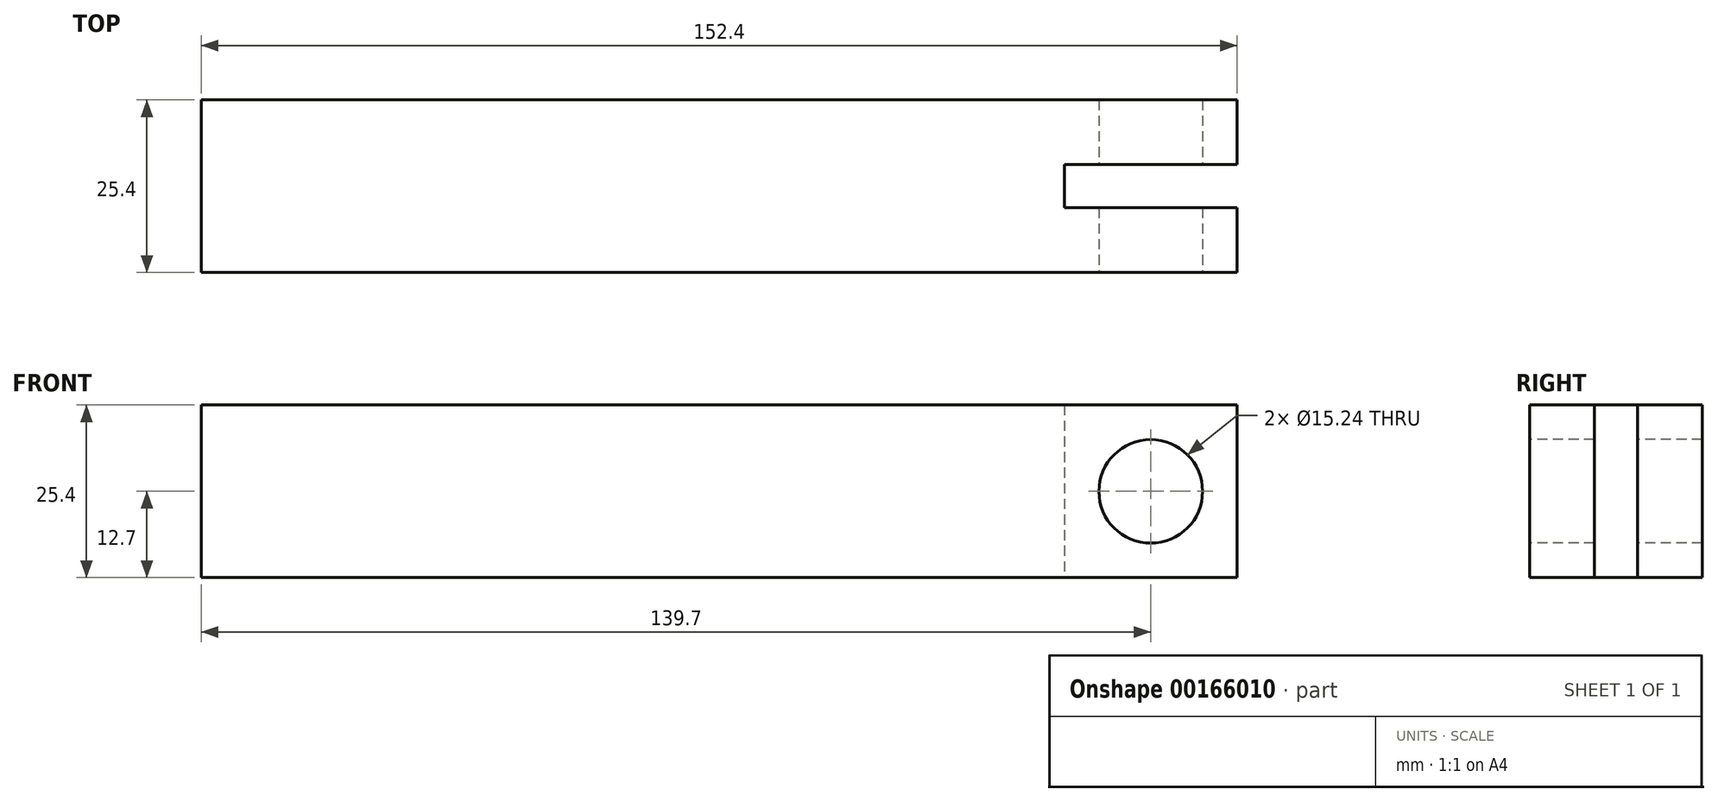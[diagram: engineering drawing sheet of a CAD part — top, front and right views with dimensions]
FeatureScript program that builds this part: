
annotation { "Feature Type Name" : "Feature", "Feature Type Description" : "" }
export const myFeature = defineFeature(function(context is Context, id is Id, definition is map)
    precondition{}
    {
        {
            var Q0;
            Q0=qCreatedBy(makeId("Right.planeOp"),FACE);
            var sketch = newSketch(context, id + "F0", { "sketchPlane" : qUnion([Q0])});
            skLineSegment(sketch, "E0.bottom", {"start": v(12.7, 12.7) * mm, "end": v(-12.7, 12.7) * mm});
            skLineSegment(sketch, "E0.top", {"start": v(12.7, -12.7) * mm, "end": v(-12.7, -12.7) * mm});
            skLineSegment(sketch, "E0.left", {"start": v(12.7, 12.7) * mm, "end": v(12.7, -12.7) * mm});
            skLineSegment(sketch, "E0.right", {"start": v(-12.7, 12.7) * mm, "end": v(-12.7, -12.7) * mm});
            skPoint(sketch, "E0.middle", {"position": v(0, 0) * mm});
            skSolve(sketch);
        }
        {
            var Q0;
            Q0 = qSketchRegion(id + "F0", true);
            extrude(context, id + "F1", {"entities" : qUnion([Q0]), "endBound" : BoundingType.SYMMETRIC, "depth" : 152.4 * mm});
        }
        {
            var Q0;
            Q0=makeQuery(id+"F1.opExtrude","SWEPT_FACE",FACE,{"disambiguationData":[OSD([sQuery(id+"F0.wireOp",EDGE,"E0.right")])]});
            var sketch = newSketch(context, id + "F2", { "sketchPlane" : qUnion([Q0])});
            skCircle(sketch, "E1", {"center": v(63.5, 0) * mm, "radius": 7.62 * mm});
            skSolve(sketch);
        }
        {
            var Q0;
            Q0 = qSketchRegion(id + "F2", true);
            extrude(context, id + "F3", {"entities" : qUnion([Q0]), "operationType" : NewBodyOperationType.REMOVE, "endBound" : BoundingType.UP_TO_NEXT, "oppositeDirection" : true, "depth" : 25.4 * mm});
        }
        {
            var Q0;
            Q0=makeQuery(id+"F1.opExtrude","CAP_FACE",FACE,{"disambiguationData":[OSD([sQuery(id+"F0.wireOp",EDGE,"E0.bottom"),sQuery(id+"F0.wireOp",EDGE,"E0.top"),sQuery(id+"F0.wireOp",EDGE,"E0.left"),sQuery(id+"F0.wireOp",EDGE,"E0.right")])],"isStart":false});
            var sketch = newSketch(context, id + "F4", { "sketchPlane" : qUnion([Q0])});
            skLineSegment(sketch, "E2.bottom", {"start": v(3.18, 12.7) * mm, "end": v(-3.18, 12.7) * mm});
            skLineSegment(sketch, "E2.top", {"start": v(3.18, -12.7) * mm, "end": v(-3.18, -12.7) * mm});
            skLineSegment(sketch, "E2.left", {"start": v(3.18, 12.7) * mm, "end": v(3.18, -12.7) * mm});
            skLineSegment(sketch, "E2.right", {"start": v(-3.18, 12.7) * mm, "end": v(-3.18, -12.7) * mm});
            skPoint(sketch, "E2.middle", {"position": v(0, 0) * mm});
            skSolve(sketch);
        }
        {
            var Q0;
            Q0 = qSketchRegion(id + "F4", true);
            extrude(context, id + "F5", {"entities" : qUnion([Q0]), "operationType" : NewBodyOperationType.REMOVE, "oppositeDirection" : true, "depth" : 25.4 * mm});
        }
    });
